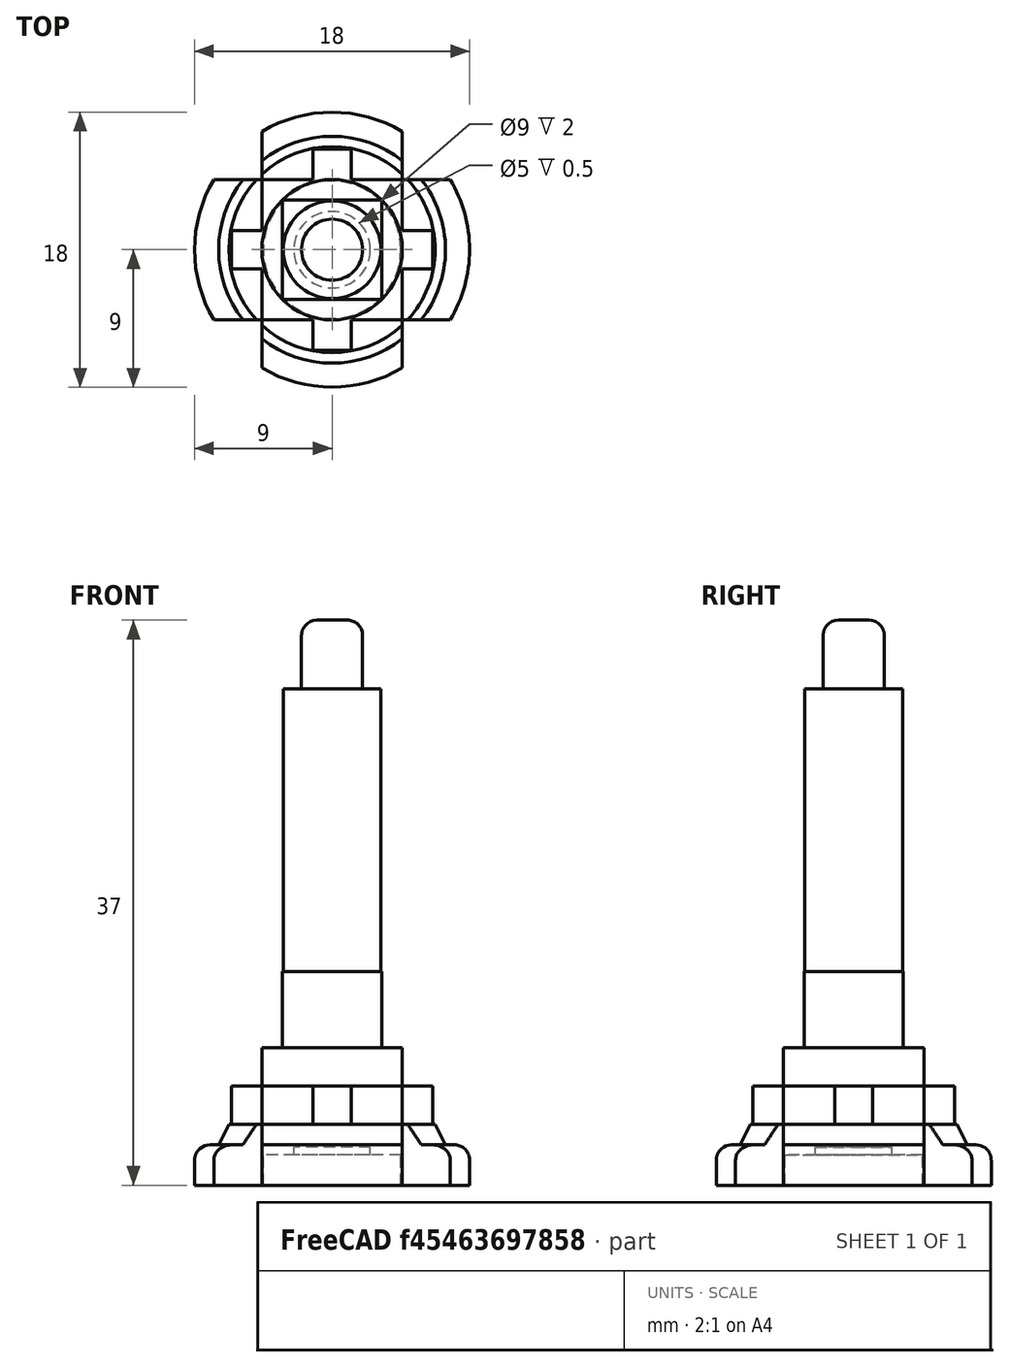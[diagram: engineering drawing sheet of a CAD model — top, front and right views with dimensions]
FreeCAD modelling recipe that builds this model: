
FCSTD DOCUMENT  (FreeCAD 0.19R24276 (Git))
Label: Tornillo
License: All rights reserved
LicenseURL: http://en.wikipedia.org/wiki/All_rights_reserved
objects: TechDraw::DrawViewDimension×15, Part::Cylinder×7, Part::Fillet×5, Part::Box×3, Part::Cut×3, Part::FeaturePython×2, Part::MultiFuse×2, TechDraw::DrawSVGTemplate×2, TechDraw::DrawViewPart×2, TechDraw::DrawProjGroupItem×2, TechDraw::DrawPage×2, Part::Cone×1, TechDraw::DrawProjGroup×1, TechDraw::DrawViewAnnotation×1
note: 23 computed .brp shape members not serialized (recipe doc carries the construction recipe); baked Part::Feature solids carry a one-line shape summary decoded from their .brp

FEATURE [Part::Cylinder] Cylinder  label="Cilindro"
  Angle = 360
  AttacherType = Attacher::AttachEngine3D
  Height = 2.65
  Placement = pos=(0,0,2) rot=(0,0,1;0rad)
  Radius = 9
FEATURE [Part::Cylinder] Cylinder001  label="Cilindro001"
  Angle = 90
  AttacherType = Attacher::AttachEngine3D
  Height = 6
  Placement = pos=(4.6,4.6,0) rot=(0,0,1;0rad)
  Radius = 9
FEATURE [Part::FeaturePython] Array  # Draft array (typed FeaturePython)
  Angle = 360
  ArrayType = 1
  Axis = (0,0,1)
  Base = -> Cylinder001
  Center = (0,0,0)
  Fuse = false
  IntervalAxis = (0,0,0)
  IntervalX = (1,0,0)
  IntervalY = (0,1,0)
  IntervalZ = (0,0,0)
  NumberPolar = 4
  NumberX = 2
  NumberY = 2
  NumberZ = 1
FEATURE [Part::Box] Box  label="Cubo"
  AttacherType = Attacher::AttachEngine3D
  Height = 2.5
  Length = 9.2
  Placement = pos=(-4.6,-4.6,6) rot=(0,0,1;0rad)
  Width = 9.2
FEATURE [Part::Box] Box001  label="Cubo001"
  AttacherType = Attacher::AttachEngine3D
  Height = 2.5
  Length = 2
  Placement = pos=(4.6,-1.25,6) rot=(0,0,1;0rad)
  Width = 2.5
FEATURE [Part::FeaturePython] Array001  # Draft array (typed FeaturePython)
  Angle = 360
  ArrayType = 1
  Axis = (0,0,1)
  Base = -> Box001
  Center = (0,0,0)
  Fuse = false
  IntervalAxis = (0,0,0)
  IntervalX = (1,0,0)
  IntervalY = (0,1,0)
  IntervalZ = (0,0,0)
  NumberPolar = 4
  NumberX = 2
  NumberY = 2
  NumberZ = 1
FEATURE [Part::Cylinder] Cylinder003  label="Cilindro003"
  Angle = 360
  AttacherType = Attacher::AttachEngine3D
  Height = 2.5
  Placement = pos=(0,0,8.5) rot=(0,0,1;0rad)
  Radius = 4.6
FEATURE [Part::Box] Box002  label="Cubo002"
  AttacherType = Attacher::AttachEngine3D
  Height = 5
  Length = 6.5
  Placement = pos=(-3.25,-3.25,11) rot=(0,0,1;0rad)
  Width = 6.5
FEATURE [Part::Cylinder] Cylinder004  label="Cilindro004"
  Angle = 360
  AttacherType = Attacher::AttachEngine3D
  Height = 18.5
  Placement = pos=(0,0,16) rot=(0,0,1;0rad)
  Radius = 3.2
FEATURE [Part::Cylinder] Cylinder005  label="Cilindro005"
  Angle = 360
  AttacherType = Attacher::AttachEngine3D
  Height = 5
  Placement = pos=(0,0,34) rot=(0,0,1;0rad)
  Radius = 2
FEATURE [Part::Cylinder] Cylinder006  label="Cilindro006"
  Angle = 360
  AttacherType = Attacher::AttachEngine3D
  Height = 2
  Placement = pos=(0,0,2) rot=(0,0,1;0rad)
  Radius = 4.5
FEATURE [Part::Cylinder] Cylinder007  label="Cilindro007"
  Angle = 360
  AttacherType = Attacher::AttachEngine3D
  Height = 6
  Placement = pos=(0,0,4) rot=(0,0,1;0rad)
  Radius = 2.5
FEATURE [Part::Cone] Cone  label="Cono"
  Angle = 360
  AttacherType = Attacher::AttachEngine3D
  Height = 1.5
  Placement = pos=(0,0,4.5) rot=(0,0,1;0rad)
  Radius1 = 7.5
  Radius2 = 6.75
FEATURE [Part::Cut] Cut
  Base = -> Cylinder
  Tool = -> Cylinder007
FEATURE [Part::Cut] Cut001
  Base = -> Cut
  Tool = -> Cylinder006
FEATURE [Part::MultiFuse] Fusion
  Shapes = -> [Cone,Cut001]
FEATURE [Part::Cut] Cut002
  Base = -> Fusion
  Tool = -> Array
FEATURE [Part::Fillet] Fillet
  Base = -> Cut002
  Edges = 1 edges r=1: [Edge66]
FEATURE [Part::Fillet] Fillet001
  Base = -> Fillet
  Edges = 1 edges r=1: [Edge69]
FEATURE [Part::Fillet] Fillet002
  Base = -> Fillet001
  Edges = 1 edges r=1: [Edge70]
FEATURE [Part::Fillet] Fillet003
  Base = -> Fillet002
  Edges = 1 edges r=1: [Edge70]
FEATURE [Part::Fillet] Fillet004
  Base = -> Cylinder005
  Edges = 1 edges r=1: [Edge1]
FEATURE [Part::MultiFuse] Fusion001
  Shapes = -> [Box,Array001,Cylinder003,Box002,Cylinder004,Fillet003,Fillet004]
FEATURE [TechDraw::DrawSVGTemplate] Template
  EditableTexts = Designed_by_Name=<owner>; Drawing_number=001; FC-Date=-; FC-SC=2:1; FC-SH=1/10; FC-Title=WeldMaskBolt; Subtitle=Tornillo; Weight=<100gr
  Height = 210
  Orientation = 1
  Width = 297
FEATURE [TechDraw::DrawSVGTemplate] Template001
  EditableTexts = Designed_by_Name=<owner>; Drawing_number=001; FC-Date=-; FC-SC=3:1; FC-SH=2/10; FC-Title=WeldMaskBolt; Subtitle=Tornillo; Weight=<100gr
  Height = 210
  Orientation = 1
  Width = 297
FEATURE [TechDraw::DrawViewPart] View
  CoarseView = false
  Direction = (0.577,-0.577,0.577)
  Focus = 100
  HardHidden = false
  IsoCount = 0
  IsoHidden = false
  IsoVisible = false
  LockPosition = false
  Perspective = false
  Rotation = 0
  Scale = 3
  ScaleType = 0
  SeamHidden = false
  SeamVisible = true
  SmoothHidden = false
  SmoothVisible = true
  Source = -> [Fusion001]
  X = 224.084
  XDirection = (0.707,0.707,0)
  Y = 134.221
FEATURE [TechDraw::DrawViewPart] View001
  CoarseView = false
  Direction = (0.577,-0.577,0.577)
  Focus = 100
  HardHidden = false
  IsoCount = 0
  IsoHidden = false
  IsoVisible = false
  LockPosition = false
  Perspective = false
  Rotation = 0
  Scale = 3
  ScaleType = 0
  SeamHidden = false
  SeamVisible = true
  SmoothHidden = false
  SmoothVisible = true
  Source = -> [Fusion001]
  X = 150.058
  XDirection = (0.707,0.707,0)
  Y = 127.987
FEATURE [TechDraw::DrawProjGroupItem] ProjItem  label="Front"
  CoarseView = false
  Direction = (0,-1,0)
  Focus = 100
  HardHidden = false
  IsoCount = 0
  IsoHidden = false
  IsoVisible = false
  LockPosition = true
  Perspective = false
  Rotation = 0
  RotationVector = (1,0,0)
  Scale = 2
  ScaleType = 2
  SeamHidden = false
  SeamVisible = true
  SmoothHidden = false
  SmoothVisible = true
  Source = -> [Fusion001]
  Type = 0
  X = 0
  XDirection = (1,0,0)
  Y = 0
FEATURE [TechDraw::DrawProjGroupItem] ProjItem002  label="Top"
  CoarseView = false
  Direction = (0,0,1)
  Focus = 100
  HardHidden = false
  IsoCount = 0
  IsoHidden = false
  IsoVisible = false
  LockPosition = false
  Perspective = false
  Rotation = 0
  RotationVector = (1,0,0)
  ScaleType = 2
  SeamHidden = false
  SeamVisible = true
  SmoothHidden = false
  SmoothVisible = true
  Source = -> [Fusion001]
  Type = 4
  X = 0
  XDirection = (1,0,0)
  Y = -108
FEATURE [TechDraw::DrawProjGroup] ProjGroup
  Anchor = -> ProjItem
  AutoDistribute = true
  LockPosition = false
  ProjectionType = 0
  Rotation = 0
  Scale = 2
  ScaleType = 2
  Source = -> [Fusion001]
  Views = -> [ProjItem,ProjItem002]
  X = 99.4091
  Y = 151.753
  spacingX = 15
  spacingY = 15
FEATURE [TechDraw::DrawViewDimension] Dimension
  Arbitrary = false
  ArbitraryTolerances = false
  EqualTolerance = true
  FormatSpec = %.2f
  FormatSpecOverTolerance = %+.2f
  FormatSpecUnderTolerance = %+.2f
  Inverted = false
  LockPosition = false
  MeasureType = 1
  OverTolerance = 0
  References2D = -> [ProjItem]
  Rotation = 0
  Scale = 3
  ScaleType = 0
  TheoreticalExact = false
  Type = 1
  UnderTolerance = 0
  X = -3.26411
  Y = -42.9277
FEATURE [TechDraw::DrawViewDimension] Dimension001
  Arbitrary = false
  ArbitraryTolerances = false
  EqualTolerance = true
  FormatSpec = %.2f
  FormatSpecOverTolerance = %+.2f
  FormatSpecUnderTolerance = %+.2f
  Inverted = false
  LockPosition = false
  MeasureType = 1
  OverTolerance = 0
  References2D = -> [ProjItem]
  Rotation = 0
  Scale = 3
  ScaleType = 0
  TheoreticalExact = false
  Type = 2
  UnderTolerance = 0
  X = -35.6249
  Y = -1.62338
FEATURE [TechDraw::DrawViewDimension] Dimension002
  Arbitrary = false
  ArbitraryTolerances = false
  EqualTolerance = true
  FormatSpec = ⌀%.2f
  FormatSpecOverTolerance = %+.2f
  FormatSpecUnderTolerance = %+.2f
  Inverted = false
  LockPosition = false
  MeasureType = 1
  OverTolerance = 0
  References2D = -> [ProjItem002]
  Rotation = 0
  Scale = 3
  ScaleType = 0
  TheoreticalExact = false
  Type = 5
  UnderTolerance = 0
  X = -49.3506
  Y = -13.6364
FEATURE [TechDraw::DrawPage] Page  label="Vistas"
  KeepUpdated = true
  NextBalloonIndex = 1
  ProjectionType = 0
  Scale = 3
  Template = -> Template
  Views = -> [View,ProjGroup,Dimension,Dimension001,Dimension002]
FEATURE [TechDraw::DrawViewDimension] Dimension003
  Arbitrary = false
  ArbitraryTolerances = false
  EqualTolerance = true
  FormatSpec = %.2f
  FormatSpecOverTolerance = %+.2f
  FormatSpecUnderTolerance = %+.2f
  Inverted = false
  LockPosition = false
  MeasureType = 1
  OverTolerance = 0
  References2D = -> [View001]
  Rotation = 0
  Scale = 2
  ScaleType = 0
  TheoreticalExact = false
  Type = 0
  UnderTolerance = 0
  X = -43.8932
  Y = 27.1001
FEATURE [TechDraw::DrawViewDimension] Dimension004
  Arbitrary = false
  ArbitraryTolerances = false
  EqualTolerance = true
  FormatSpec = ⌀%.2f
  FormatSpecOverTolerance = %+.2f
  FormatSpecUnderTolerance = %+.2f
  Inverted = false
  LockPosition = false
  MeasureType = 1
  OverTolerance = 0
  References2D = -> [View001]
  Rotation = 0
  Scale = 2
  ScaleType = 0
  TheoreticalExact = false
  Type = 5
  UnderTolerance = 0
  X = -2.00884
  Y = -12.1413
FEATURE [TechDraw::DrawViewDimension] Dimension005
  Arbitrary = false
  ArbitraryTolerances = false
  EqualTolerance = true
  FormatSpec = %.2f
  FormatSpecOverTolerance = %+.2f
  FormatSpecUnderTolerance = %+.2f
  Inverted = false
  LockPosition = false
  MeasureType = 1
  OverTolerance = 0
  References2D = -> [View001]
  Rotation = 0
  Scale = 2
  ScaleType = 0
  TheoreticalExact = false
  Type = 0
  UnderTolerance = 0
  X = 31.738
  Y = -50.198
FEATURE [TechDraw::DrawViewDimension] Dimension006
  Arbitrary = false
  ArbitraryTolerances = false
  EqualTolerance = true
  FormatSpec = %.2f
  FormatSpecOverTolerance = %+.2f
  FormatSpecUnderTolerance = %+.2f
  Inverted = false
  LockPosition = false
  MeasureType = 1
  OverTolerance = 0
  References2D = -> [View001]
  Rotation = 0
  Scale = 2
  ScaleType = 0
  TheoreticalExact = false
  Type = 0
  UnderTolerance = 0
  X = 31.7388
  Y = -8.7968
FEATURE [TechDraw::DrawViewDimension] Dimension007
  Arbitrary = false
  ArbitraryTolerances = false
  EqualTolerance = true
  FormatSpec = %.2f
  FormatSpecOverTolerance = %+.2f
  FormatSpecUnderTolerance = %+.2f
  Inverted = false
  LockPosition = false
  MeasureType = 1
  OverTolerance = 0
  References2D = -> [View001]
  Rotation = 0
  Scale = 2
  ScaleType = 0
  TheoreticalExact = false
  Type = 2
  UnderTolerance = 0
  X = -53.5132
  Y = -48.7118
FEATURE [TechDraw::DrawViewDimension] Dimension008
  Arbitrary = false
  ArbitraryTolerances = false
  EqualTolerance = true
  FormatSpec = %.2f
  FormatSpecOverTolerance = %+.2f
  FormatSpecUnderTolerance = %+.2f
  Inverted = false
  LockPosition = false
  MeasureType = 1
  OverTolerance = 0
  References2D = -> [View001]
  Rotation = 0
  Scale = 2
  ScaleType = 0
  TheoreticalExact = false
  Type = 6
  UnderTolerance = 0
  X = 1.32721
  Y = -61.3636
FEATURE [TechDraw::DrawViewDimension] Dimension009
  Arbitrary = false
  ArbitraryTolerances = false
  EqualTolerance = true
  FormatSpec = ⌀%.2f
  FormatSpecOverTolerance = %+.2f
  FormatSpecUnderTolerance = %+.2f
  Inverted = false
  LockPosition = false
  MeasureType = 1
  OverTolerance = 0
  References2D = -> [View001]
  Rotation = 0
  Scale = 2
  ScaleType = 0
  TheoreticalExact = false
  Type = 5
  UnderTolerance = 0
  X = -67.9768
  Y = -14.3848
FEATURE [TechDraw::DrawViewDimension] Dimension010
  Arbitrary = false
  ArbitraryTolerances = false
  EqualTolerance = true
  FormatSpec = %.2f
  FormatSpecOverTolerance = %+.2f
  FormatSpecUnderTolerance = %+.2f
  Inverted = false
  LockPosition = false
  MeasureType = 1
  OverTolerance = 0
  References2D = -> [View001]
  Rotation = 0
  Scale = 2
  ScaleType = 0
  TheoreticalExact = false
  Type = 0
  UnderTolerance = 0
  X = -34.0425
  Y = -59.9533
FEATURE [TechDraw::DrawViewDimension] Dimension011
  Arbitrary = false
  ArbitraryTolerances = false
  EqualTolerance = true
  FormatSpec = %.2f
  FormatSpecOverTolerance = %+.2f
  FormatSpecUnderTolerance = %+.2f
  Inverted = false
  LockPosition = false
  MeasureType = 1
  OverTolerance = 0
  References2D = -> [View001]
  Rotation = 0
  Scale = 2
  ScaleType = 0
  TheoreticalExact = false
  Type = 0
  UnderTolerance = 0
  X = -20.6896
  Y = -37.8434
FEATURE [TechDraw::DrawViewDimension] Dimension012
  Arbitrary = false
  ArbitraryTolerances = false
  EqualTolerance = true
  FormatSpec = ⌀%.2f
  FormatSpecOverTolerance = %+.2f
  FormatSpecUnderTolerance = %+.2f
  Inverted = false
  LockPosition = false
  MeasureType = 1
  OverTolerance = 0
  References2D = -> [View001]
  Rotation = 0
  Scale = 2
  ScaleType = 0
  TheoreticalExact = false
  Type = 5
  UnderTolerance = 0
  X = -42.6852
  Y = 38.6702
FEATURE [TechDraw::DrawViewDimension] Dimension013
  Arbitrary = false
  ArbitraryTolerances = false
  EqualTolerance = true
  FormatSpec = %.2f
  FormatSpecOverTolerance = %+.2f
  FormatSpecUnderTolerance = %+.2f
  Inverted = false
  LockPosition = false
  MeasureType = 1
  OverTolerance = 0
  References2D = -> [View001]
  Rotation = 0
  Scale = 2
  ScaleType = 0
  TheoreticalExact = false
  Type = 2
  UnderTolerance = 0
  X = 40.7997
  Y = 42.0136
FEATURE [TechDraw::DrawViewDimension] Dimension014
  Arbitrary = false
  ArbitraryTolerances = false
  EqualTolerance = true
  FormatSpec = ⌀%.2f
  FormatSpecOverTolerance = %+.2f
  FormatSpecUnderTolerance = %+.2f
  Inverted = false
  LockPosition = false
  MeasureType = 1
  OverTolerance = 0
  References2D = -> [View001]
  Rotation = 0
  Scale = 2
  ScaleType = 0
  TheoreticalExact = false
  Type = 5
  UnderTolerance = 0
  X = -47.968
  Y = 47.968
FEATURE [TechDraw::DrawViewAnnotation] Annotation
  Font = osifont
  LineSpace = 80
  LockPosition = false
  MaxWidth = -1
  Rotation = 0
  Scale = 2
  ScaleType = 0
  Text = Aproximate measurements: | Check with 3D piece
  TextSize = 5
  TextStyle = 0
  X = 54.8075
  Y = 84.4516
FEATURE [TechDraw::DrawPage] Page001  label="Cotas"
  KeepUpdated = true
  NextBalloonIndex = 1
  ProjectionType = 0
  Scale = 2
  Template = -> Template001
  Views = -> [View001,Dimension003,Dimension004,Dimension005,Dimension006,Dimension007,Dimension008,Dimension009,Dimension010,Dimension011,Dimension012,Dimension013,Dimension014,Annotation]
